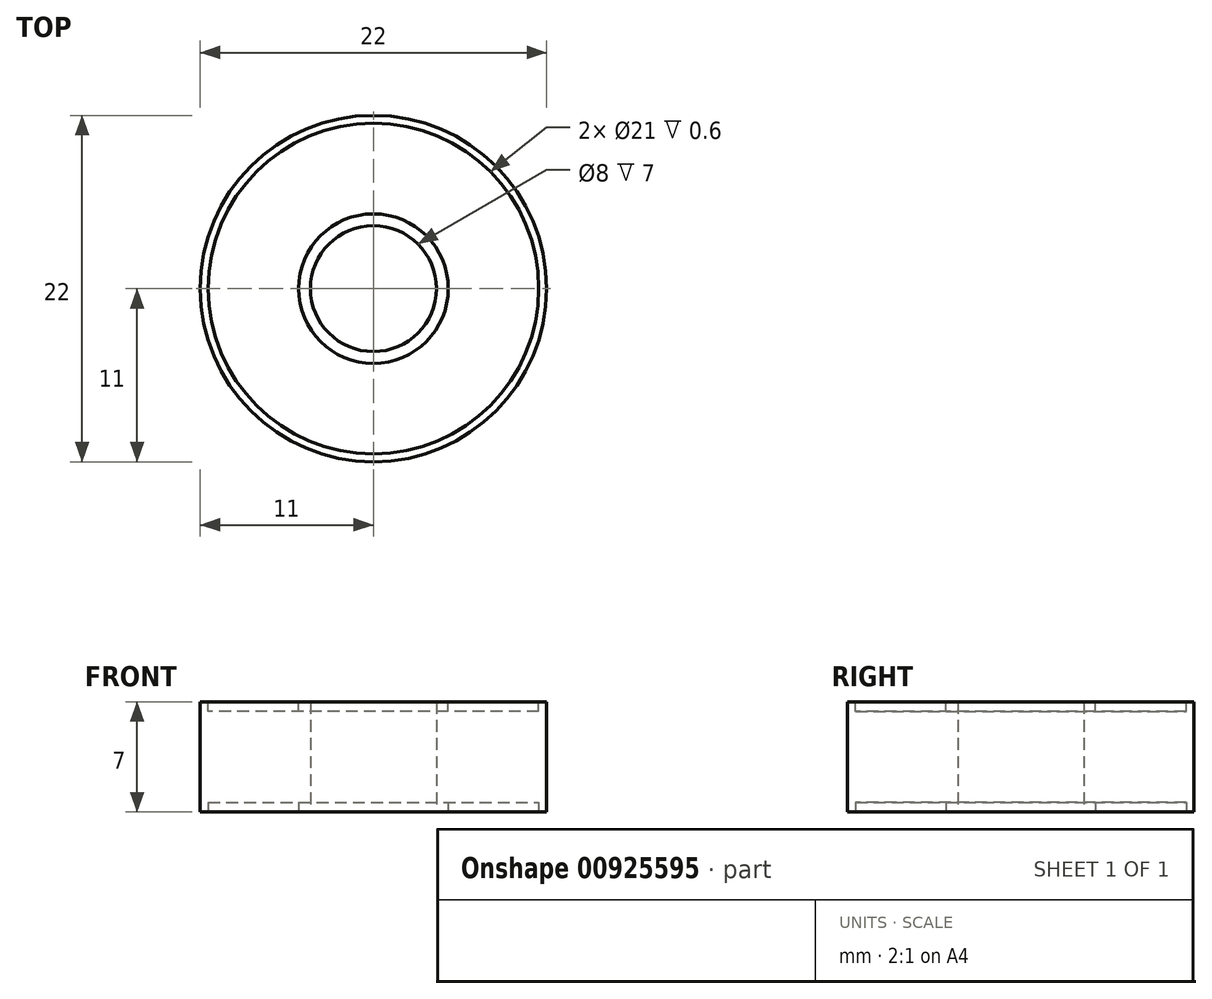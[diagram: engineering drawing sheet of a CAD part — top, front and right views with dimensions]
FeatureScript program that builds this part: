
annotation { "Feature Type Name" : "Feature", "Feature Type Description" : "" }
export const myFeature = defineFeature(function(context is Context, id is Id, definition is map)
    precondition{}
    {
        {
            var Q0;
            Q0=qCreatedBy(makeId("Top.planeOp"),FACE);
            var sketch = newSketch(context, id + "F0", { "sketchPlane" : qUnion([Q0])});
            skCircle(sketch, "E0", {"center": v(0, 0) * mm, "radius": 11 * mm});
            skCircle(sketch, "E1", {"center": v(0, 0) * mm, "radius": 4 * mm});
            skSolve(sketch);
        }
        {
            var Q0;
            Q0 = qSketchRegion(id + "F0", true);
            extrude(context, id + "F1", {"entities" : qUnion([Q0]), "depth" : 7 * mm, "offsetDistance" : 25 * mm});
        }
        {
            var Q0;
            Q0=makeQuery(id+"F1.opExtrude","CAP_FACE",FACE,{"disambiguationData":[OSD([sQuery(id+"F0.wireOp",EDGE,"E0"),sQuery(id+"F0.wireOp",EDGE,"E1")])],"isStart":false});
            var sketch = newSketch(context, id + "F2", { "sketchPlane" : qUnion([Q0])});
            skCircle(sketch, "E2", {"center": v(0, 0) * mm, "radius": 4.75 * mm});
            skCircle(sketch, "E3", {"center": v(0, 0) * mm, "radius": 10.5 * mm});
            skSolve(sketch);
        }
        {
            var Q0;
            Q0 = qSketchRegion(id + "F2", true);
            extrude(context, id + "F3", {"entities" : qUnion([Q0]), "operationType" : NewBodyOperationType.REMOVE, "oppositeDirection" : true, "depth" : .6 * mm, "offsetDistance" : 25 * mm});
        }
        {
            var Q0;
            Q0=makeQuery(id+"F1.opExtrude","CAP_FACE",FACE,{"disambiguationData":[OSD([sQuery(id+"F0.wireOp",EDGE,"E0"),sQuery(id+"F0.wireOp",EDGE,"E1")])],"isStart":true});
            var sketch = newSketch(context, id + "F4", { "sketchPlane" : qUnion([Q0])});
            skCircle(sketch, "E4", {"center": v(0, 0) * mm, "radius": 4.75 * mm});
            skCircle(sketch, "E5", {"center": v(0, 0) * mm, "radius": 10.5 * mm});
            skSolve(sketch);
        }
        {
            var Q0;
            Q0 = qSketchRegion(id + "F4", true);
            extrude(context, id + "F5", {"entities" : qUnion([Q0]), "operationType" : NewBodyOperationType.REMOVE, "oppositeDirection" : true, "depth" : .6 * mm, "offsetDistance" : 25 * mm});
        }
    });
